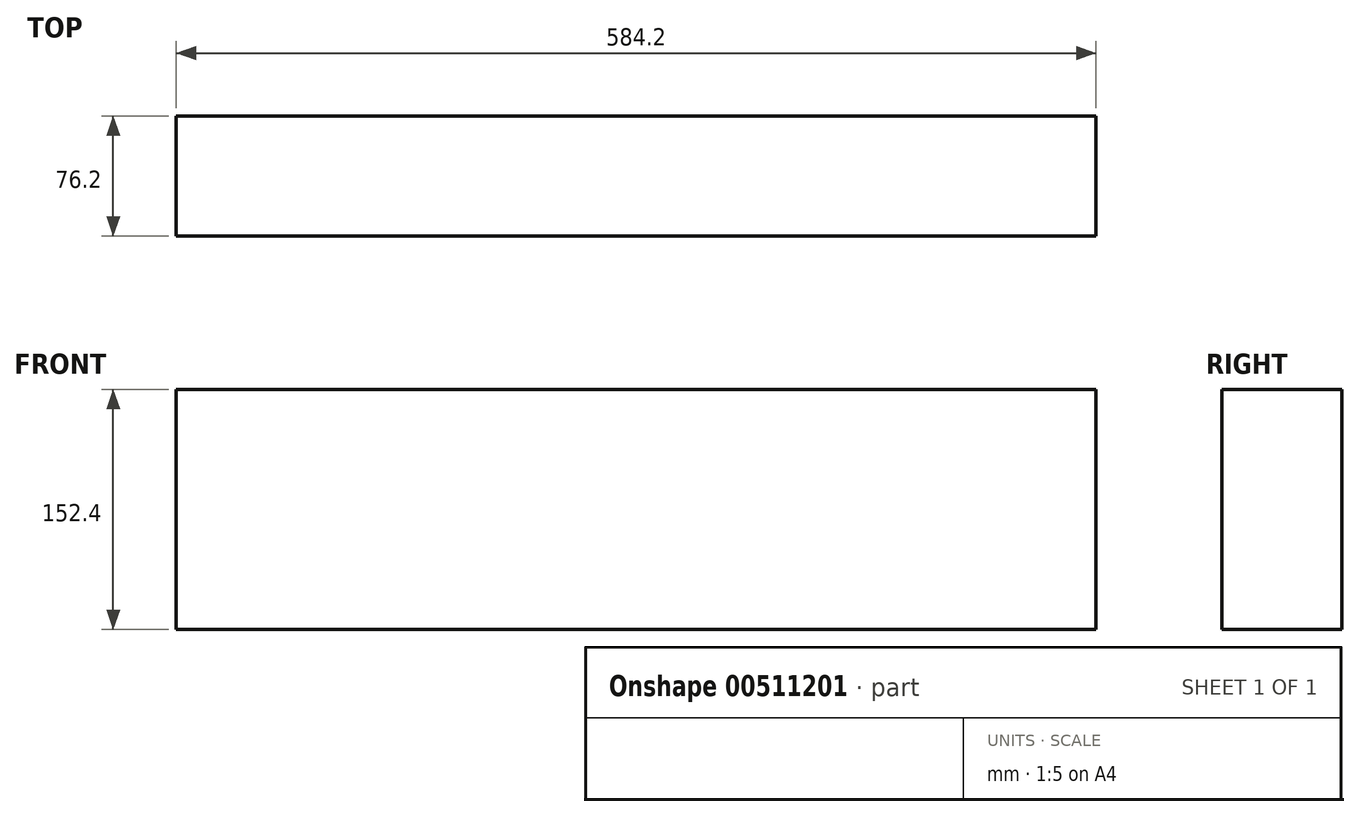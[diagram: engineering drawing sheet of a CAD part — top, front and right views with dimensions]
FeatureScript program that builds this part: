
annotation { "Feature Type Name" : "Feature", "Feature Type Description" : "" }
export const myFeature = defineFeature(function(context is Context, id is Id, definition is map)
    precondition{}
    {
        {
            var Q0;
            Q0=qCreatedBy(makeId("Front.planeOp"),FACE);
            var sketch = newSketch(context, id + "F0", { "sketchPlane" : qUnion([Q0])});
            skLineSegment(sketch, "E0.bottom", {"start": v(-292.1, 76.2) * mm, "end": v(292.1, 76.2) * mm});
            skLineSegment(sketch, "E0.top", {"start": v(-292.1, -76.2) * mm, "end": v(292.1, -76.2) * mm});
            skLineSegment(sketch, "E0.left", {"start": v(-292.1, 76.2) * mm, "end": v(-292.1, -76.2) * mm});
            skLineSegment(sketch, "E0.right", {"start": v(292.1, 76.2) * mm, "end": v(292.1, -76.2) * mm});
            skPoint(sketch, "E0.middle", {"position": v(0, 0) * mm});
            skSolve(sketch);
        }
        {
            var Q0;
            Q0 = qSketchRegion(id + "F0", true);
            extrude(context, id + "F1", {"entities" : qUnion([Q0]), "endBound" : BoundingType.SYMMETRIC, "depth" : 76.2 * mm});
        }
    });
